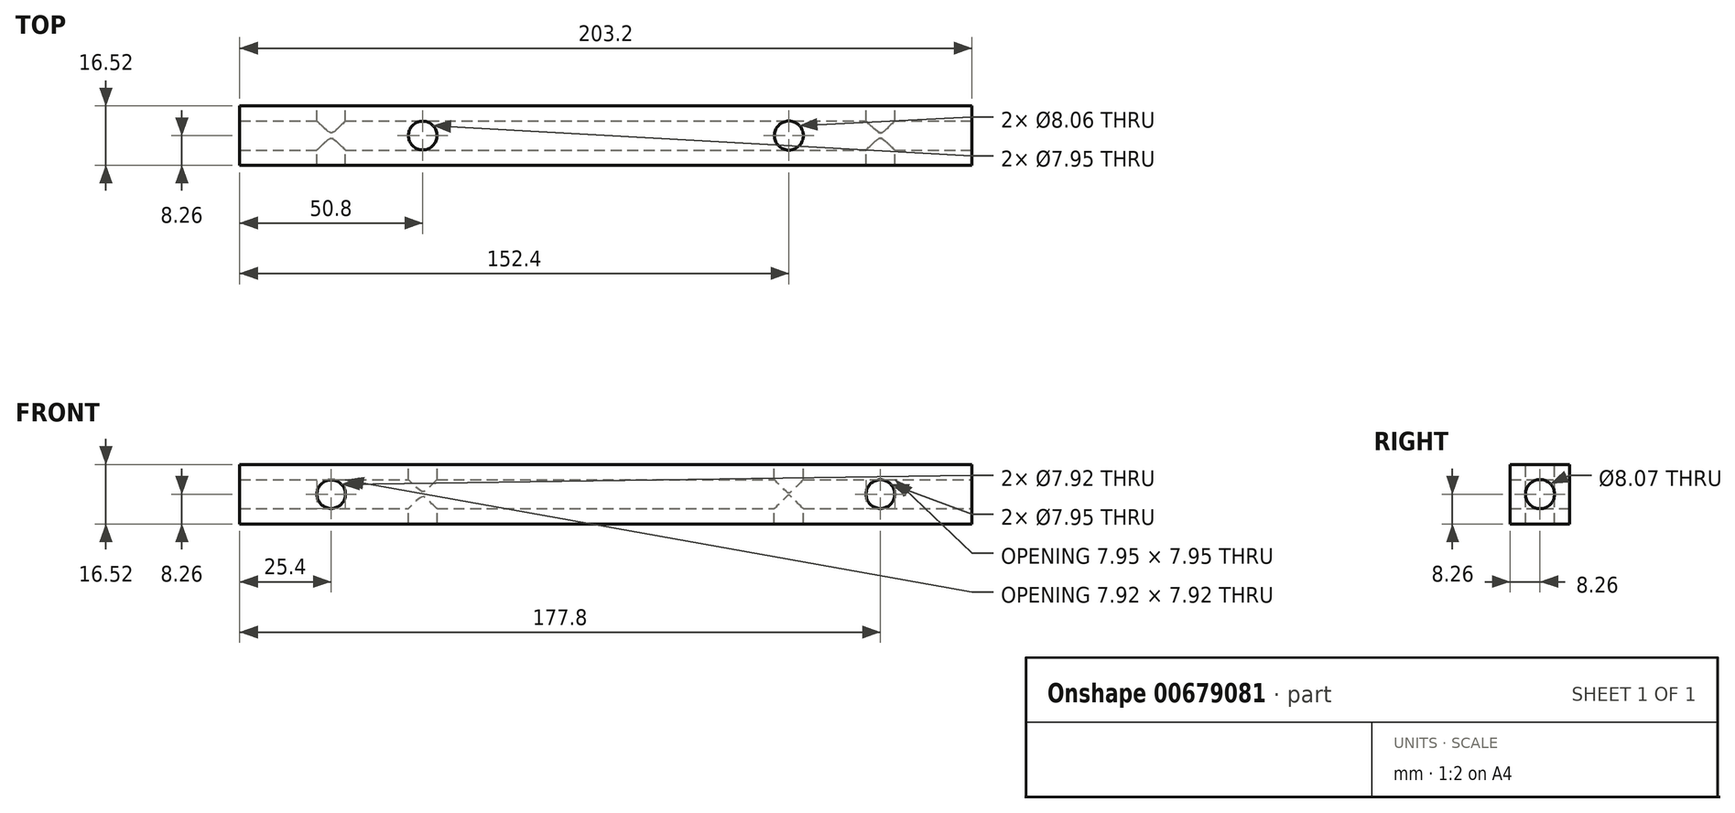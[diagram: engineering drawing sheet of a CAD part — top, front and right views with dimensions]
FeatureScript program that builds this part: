
annotation { "Feature Type Name" : "Feature", "Feature Type Description" : "" }
export const myFeature = defineFeature(function(context is Context, id is Id, definition is map)
    precondition{}
    {
        {
            var Q0;
            Q0=qCreatedBy(makeId("Front.planeOp"),FACE);
            var sketch = newSketch(context, id + "F0", { "sketchPlane" : qUnion([Q0])});
            skLineSegment(sketch, "E0.bottom", {"start": v(-101.6, 8.25) * mm, "end": v(101.6, 8.25) * mm});
            skLineSegment(sketch, "E0.top", {"start": v(-101.6, -8.25) * mm, "end": v(101.6, -8.25) * mm});
            skLineSegment(sketch, "E0.left", {"start": v(-101.6, 8.25) * mm, "end": v(-101.6, -8.25) * mm});
            skLineSegment(sketch, "E0.right", {"start": v(101.6, 8.25) * mm, "end": v(101.6, -8.25) * mm});
            skPoint(sketch, "E0.middle", {"position": v(0, 0) * mm});
            skCircle(sketch, "E1", {"center": v(-76.2, 0) * mm, "radius": 3.96 * mm});
            skCircle(sketch, "E2", {"center": v(76.2, 0) * mm, "radius": 3.97 * mm});
            skSolve(sketch);
        }
        {
            var Q0;
            Q0=qCreatedBy(makeId("Right.planeOp"),FACE);
            var sketch = newSketch(context, id + "F1", { "sketchPlane" : qUnion([Q0])});
            skCircle(sketch, "E3", {"center": v(0, 0) * mm, "radius": 4.04 * mm});
            skSolve(sketch);
        }
        {
            var Q0;
            Q0 = qSketchRegion(id + "F0", true);
            extrude(context, id + "F2", {"entities" : qUnion([Q0]), "endBound" : BoundingType.SYMMETRIC, "depth" : 16.5 * mm, "offsetDistance" : 25.4 * mm});
        }
        {
            var Q0;
            Q0 = qSketchRegion(id + "F1", true);
            extrude(context, id + "F3", {"entities" : qUnion([Q0]), "operationType" : NewBodyOperationType.REMOVE, "endBound" : BoundingType.SYMMETRIC, "oppositeDirection" : true, "depth" : 203.2 * mm, "offsetDistance" : 25.4 * mm});
        }
        {
            var Q0;
            Q0=qCreatedBy(makeId("Top.planeOp"),FACE);
            var sketch = newSketch(context, id + "F4", { "sketchPlane" : qUnion([Q0])});
            skCircle(sketch, "E4", {"center": v(-50.8, 0) * mm, "radius": 3.98 * mm});
            skCircle(sketch, "E5", {"center": v(50.8, 0) * mm, "radius": 4.03 * mm});
            skSolve(sketch);
        }
        {
            var Q0;
            Q0 = qSketchRegion(id + "F4", true);
            extrude(context, id + "F5", {"entities" : qUnion([Q0]), "operationType" : NewBodyOperationType.REMOVE, "endBound" : BoundingType.SYMMETRIC, "oppositeDirection" : true, "depth" : 16.5 * mm, "offsetDistance" : 25.4 * mm});
        }
    });
